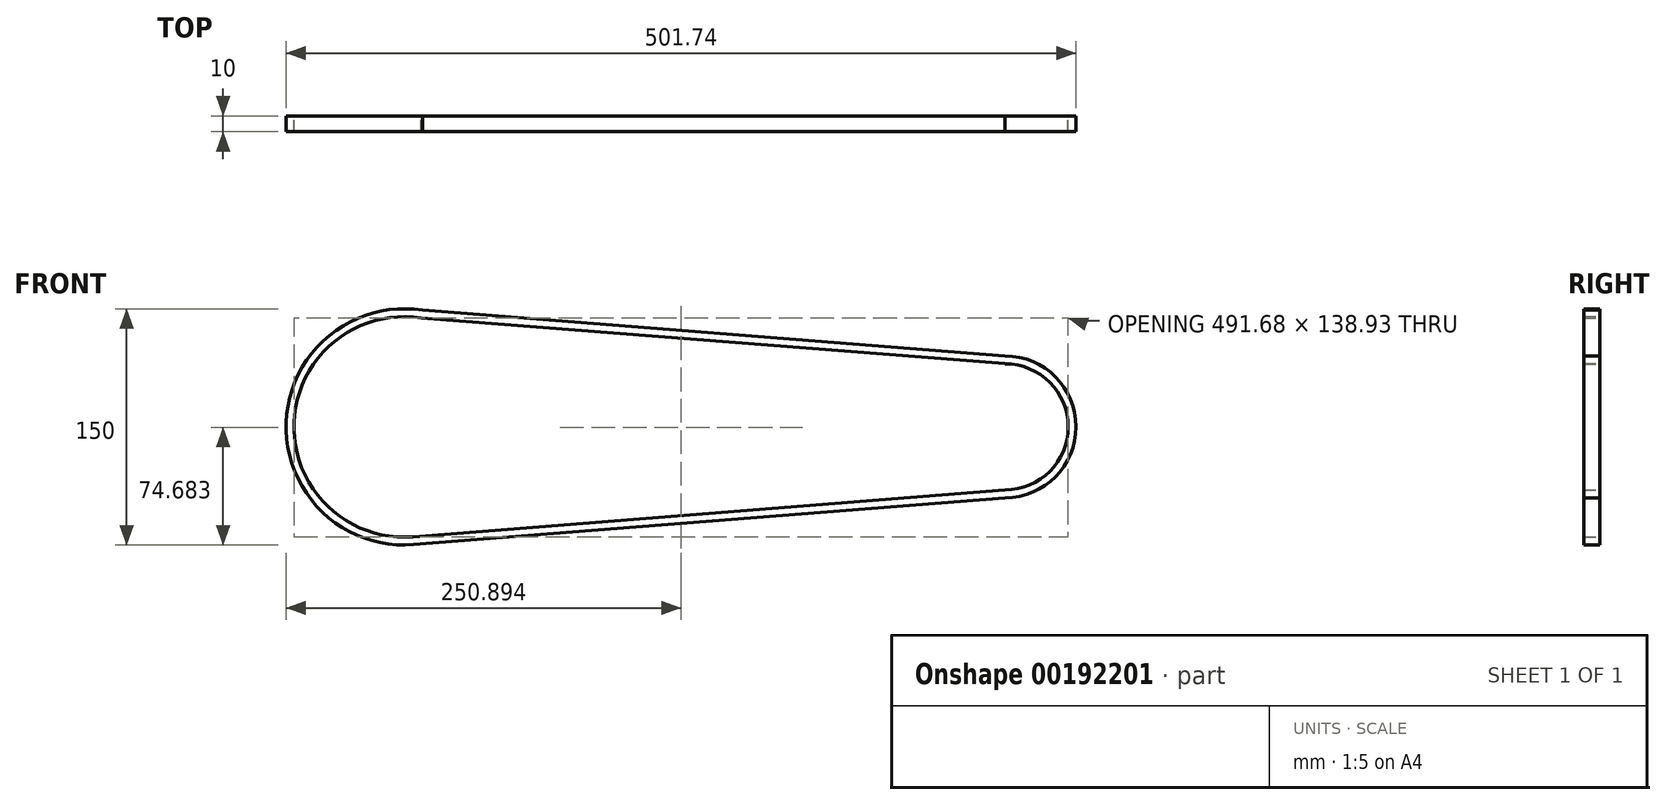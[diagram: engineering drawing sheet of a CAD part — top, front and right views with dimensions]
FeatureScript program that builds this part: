
annotation { "Feature Type Name" : "Feature", "Feature Type Description" : "" }
export const myFeature = defineFeature(function(context is Context, id is Id, definition is map)
    precondition{}
    {
        {
            var Q0;
            Q0=qCreatedBy(makeId("Front.planeOp"),FACE);
            var sketch = newSketch(context, id + "F0", { "sketchPlane" : qUnion([Q0])});
            skArc(sketch, "E0", {"start": v(11.66, 74.09) * mm, "mid": v(-74.94, 2.9) * mm, "end": v(5.92, -74.77) * mm});
            skArc(sketch, "E1", {"start": v(381.74, -45) * mm, "mid": v(426.74, 0) * mm, "end": v(381.74, 45) * mm});
            skLineSegment(sketch, "E2", {"start": v(0, 0) * mm, "end": v(0, 75) * mm});
            skLineSegment(sketch, "E3", {"start": v(0, 75) * mm, "end": v(381.74, 45.14) * mm});
            skLineSegment(sketch, "E4", {"start": v(381.74, 45.14) * mm, "end": v(381.74, 45) * mm});
            skLineSegment(sketch, "E5", {"start": v(381.74, -45) * mm, "end": v(0, -75.23) * mm});
            skArc(sketch, "E6", {"start": v(10.9, 69.15) * mm, "mid": v(-69.95, 2.7) * mm, "end": v(5.52, -69.78) * mm});
            skArc(sketch, "E7", {"start": v(381.74, -40) * mm, "mid": v(421.74, 0) * mm, "end": v(381.74, 40) * mm});
            skLineSegment(sketch, "E8", {"start": v(0, 70) * mm, "end": v(381.74, 40.12) * mm});
            skLineSegment(sketch, "E9", {"start": v(381.74, 40.12) * mm, "end": v(381.74, 40) * mm});
            skLineSegment(sketch, "E10", {"start": v(381.74, -40) * mm, "end": v(0, -70.22) * mm});
            skSolve(sketch);
        }
        {
            var Q0;
            Q0 = qSketchRegion(id + "F0", true);
            extrude(context, id + "F1", {"entities" : qUnion([Q0]), "depth" : 10 * mm, "symmetric" : true});
        }
    });
